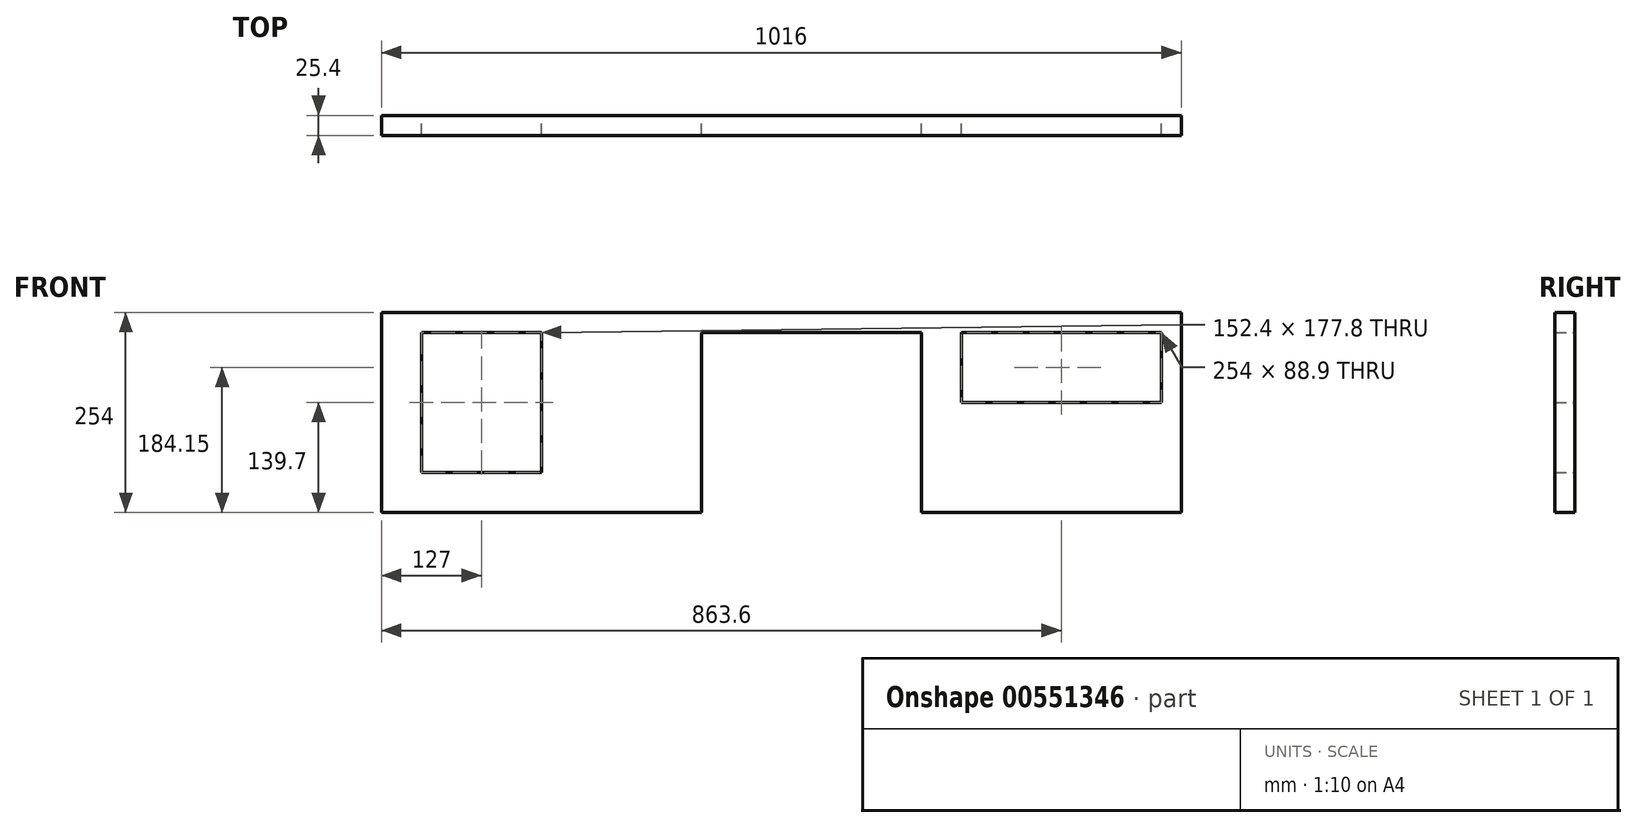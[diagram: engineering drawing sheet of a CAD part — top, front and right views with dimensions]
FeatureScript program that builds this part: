
annotation { "Feature Type Name" : "Feature", "Feature Type Description" : "" }
export const myFeature = defineFeature(function(context is Context, id is Id, definition is map)
    precondition{}
    {
        {
            var Q0;
            Q0=qCreatedBy(makeId("Front.planeOp"),FACE);
            var sketch = newSketch(context, id + "F0", { "sketchPlane" : qUnion([Q0])});
            skLineSegment(sketch, "E0.bottom", {"start": v(508, 127) * mm, "end": v(-508, 127) * mm});
            skLineSegment(sketch, "E0.top", {"start": v(508, -127) * mm, "end": v(-508, -127) * mm});
            skLineSegment(sketch, "E0.left", {"start": v(508, 127) * mm, "end": v(508, -127) * mm});
            skLineSegment(sketch, "E0.right", {"start": v(-508, 127) * mm, "end": v(-508, -127) * mm});
            skPoint(sketch, "E0.middle", {"position": v(0, 0) * mm});
            skSolve(sketch);
        }
        {
            var Q0;
            Q0=makeQuery(id+"F0.imprint","IMPRINT",FACE,{"disambiguationData":[TD([[makeQuery(id+"F0.imprint","IMPRINT",EDGE,{"derivedFrom":sQuery(id+"F0.wireOp",EDGE,"E0.bottom")}),1.0]])]});
            extrude(context, id + "F1", {"entities" : qUnion([Q0]), "depth" : 25.4 * mm, "offsetDistance" : 25.4 * mm});
        }
        {
            var Q0;
            Q0=makeQuery(id+"F1.opExtrude","CAP_FACE",FACE,{"disambiguationData":[OSD([sQuery(id+"F0.wireOp",EDGE,"E0.bottom"),sQuery(id+"F0.wireOp",EDGE,"E0.top"),sQuery(id+"F0.wireOp",EDGE,"E0.left"),sQuery(id+"F0.wireOp",EDGE,"E0.right")])],"isStart":true});
            var sketch = newSketch(context, id + "F2", { "sketchPlane" : qUnion([Q0])});
            skLineSegment(sketch, "E1", {"start": v(-203.2, 127) * mm, "end": v(-203.2, -127) * mm});
            skLineSegment(sketch, "E2", {"start": v(127, 127) * mm, "end": v(127, -127) * mm});
            skLineSegment(sketch, "E3.bottom", {"start": v(-482.6, 101.6) * mm, "end": v(-228.6, 101.6) * mm});
            skLineSegment(sketch, "E3.top", {"start": v(-482.6, 12.7) * mm, "end": v(-228.6, 12.7) * mm});
            skLineSegment(sketch, "E3.left", {"start": v(-482.6, 101.6) * mm, "end": v(-482.6, 12.7) * mm});
            skLineSegment(sketch, "E3.right", {"start": v(-228.6, 101.6) * mm, "end": v(-228.6, 12.7) * mm});
            skLineSegment(sketch, "E4.bottom", {"start": v(-177.8, 101.6) * mm, "end": v(101.6, 101.6) * mm});
            skLineSegment(sketch, "E4.top", {"start": v(-177.8, -127) * mm, "end": v(101.6, -127) * mm});
            skLineSegment(sketch, "E4.left", {"start": v(-177.8, 101.6) * mm, "end": v(-177.8, -127) * mm});
            skLineSegment(sketch, "E4.right", {"start": v(101.6, 101.6) * mm, "end": v(101.6, -127) * mm});
            skLineSegment(sketch, "E5.bottom", {"start": v(304.8, 101.6) * mm, "end": v(457.2, 101.6) * mm});
            skLineSegment(sketch, "E5.top", {"start": v(304.8, -76.2) * mm, "end": v(457.2, -76.2) * mm});
            skLineSegment(sketch, "E5.left", {"start": v(304.8, 101.6) * mm, "end": v(304.8, -76.2) * mm});
            skLineSegment(sketch, "E5.right", {"start": v(457.2, 101.6) * mm, "end": v(457.2, -76.2) * mm});
            skSolve(sketch);
        }
        {
            var Q0;
            Q0=makeQuery(id+"F2.imprint","IMPRINT",FACE,{"disambiguationData":[TD([[makeQuery(id+"F2.imprint","IMPRINT",EDGE,{"derivedFrom":sQuery(id+"F2.wireOp",EDGE,"E3.bottom")}),-1.0]])]});
            var Q1;
            Q1=makeQuery(id+"F2.imprint","IMPRINT",FACE,{"disambiguationData":[TD([[makeQuery(id+"F2.imprint","IMPRINT",EDGE,{"derivedFrom":sQuery(id+"F2.wireOp",EDGE,"E4.bottom")}),-1.0]])]});
            var Q2;
            Q2=makeQuery(id+"F2.imprint","IMPRINT",FACE,{"disambiguationData":[TD([[makeQuery(id+"F2.imprint","IMPRINT",EDGE,{"derivedFrom":sQuery(id+"F2.wireOp",EDGE,"E5.bottom")}),-1.0]])]});
            extrude(context, id + "F3", {"entities" : qUnion([Q0, Q1, Q2]), "operationType" : NewBodyOperationType.REMOVE, "oppositeDirection" : true, "depth" : 76.2 * mm, "offsetDistance" : 25.4 * mm});
        }
    });
